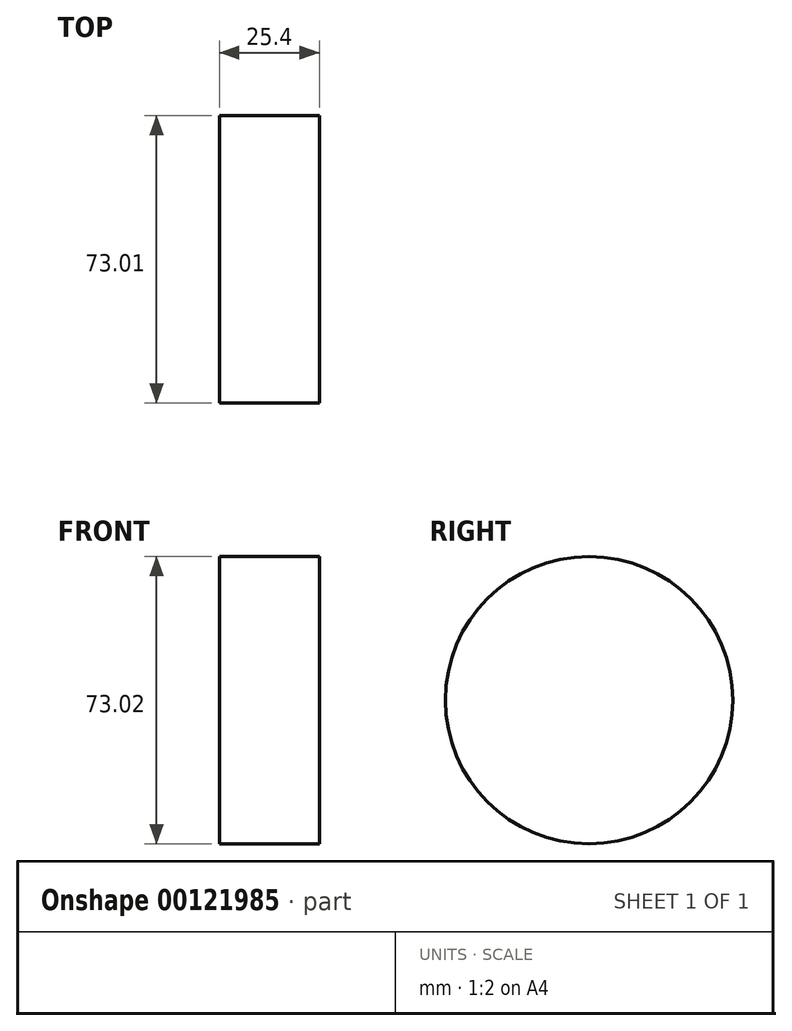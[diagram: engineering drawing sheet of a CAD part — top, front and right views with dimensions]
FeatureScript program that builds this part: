
annotation { "Feature Type Name" : "Feature", "Feature Type Description" : "" }
export const myFeature = defineFeature(function(context is Context, id is Id, definition is map)
    precondition{}
    {
        {
            var Q0;
            Q0=qCreatedBy(makeId("Right.planeOp"),FACE);
            var sketch = newSketch(context, id + "F0", { "sketchPlane" : qUnion([Q0])});
            skCircle(sketch, "E0", {"center": v(-93.68, 106.96) * mm, "radius": 36.5 * mm});
            skSolve(sketch);
        }
        {
            var Q0;
            Q0 = qSketchRegion(id + "F0", true);
            extrude(context, id + "F1", {"entities" : qUnion([Q0]), "depth" : 25.4 * mm});
        }
    });
